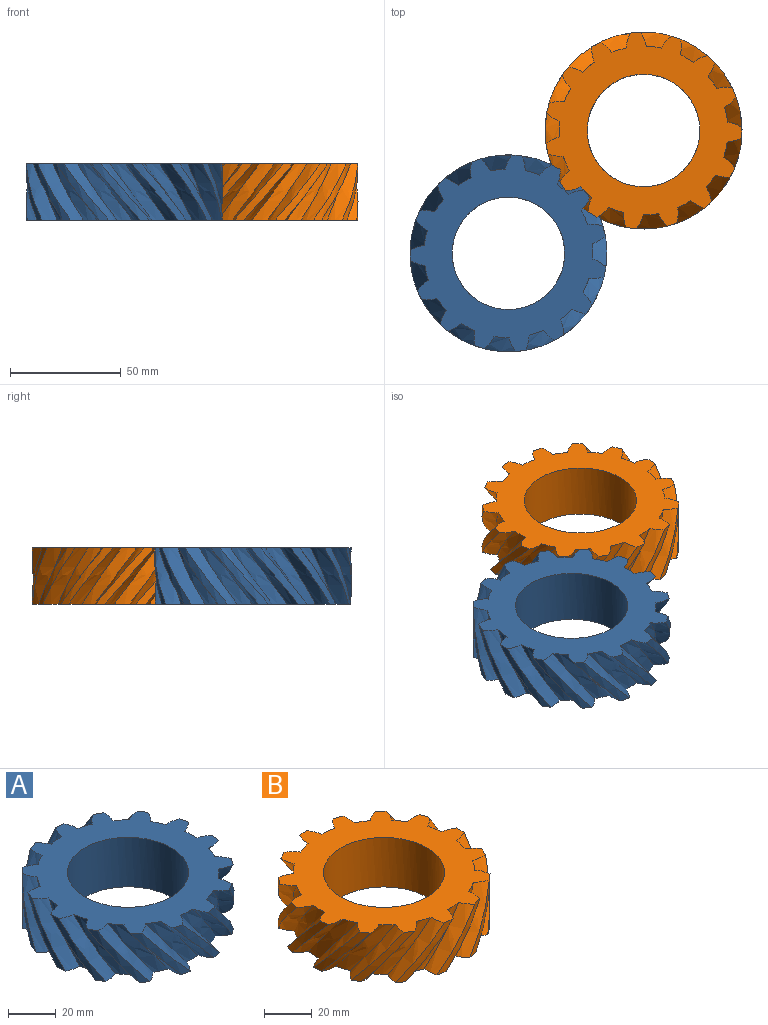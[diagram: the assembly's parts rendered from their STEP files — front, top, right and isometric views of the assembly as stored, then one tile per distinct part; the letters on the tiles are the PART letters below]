
ASSEMBLY  parts=2 mates=1
PART A: 63 faces, bbox 89.7x89.7x26.5 mm
  f0: plane 88.78x88.3mm, normal (0,0,-1), area 3229.3mm2, adj f2,f3,f4,f5,f6,f7,f8,f9
  f1: plane 88.77x88.47mm, normal (0,0,1), area 3228.8mm2, adj f2,f3,f4,f5,f6,f7,f8,f9
  f2: bspline ~26.46x18.66mm, area 176mm2, adj f0,f1,f3,f61
  f3: bspline ~25.4x18.83mm, area 220.5mm2, adj f0,f1,f2,f4
  f4: bspline ~26.46x22.91mm, area 114mm2, adj f0,f1,f3,f5
  f5: bspline ~26.46x24.18mm, area 222.2mm2, adj f0,f1,f4,f6
  f6: bspline ~26.46x24.6mm, area 176mm2, adj f0,f1,f5,f7
  f7: bspline ~26.46x22.82mm, area 220.5mm2, adj f0,f1,f6,f8
  f8: bspline ~26.98x26.46mm, area 114mm2, adj f0,f1,f7,f9
  f9: bspline ~26.46x24.53mm, area 222.2mm2, adj f0,f1,f8,f10
  f10: bspline ~26.46x26.28mm, area 176mm2, adj f0,f1,f9,f11
  f11: bspline ~26.46x24.66mm, area 220.5mm2, adj f0,f1,f10,f12
  f12: bspline ~26.46x26.38mm, area 114mm2, adj f0,f1,f11,f13
  f13: bspline ~25.4x20.98mm, area 222.2mm2, adj f0,f1,f12,f14
  f14: bspline ~26.46x23.42mm, area 176mm2, adj f0,f1,f13,f15
  f15: bspline ~26.46x23.23mm, area 220.5mm2, adj f0,f1,f14,f16
  f16: bspline ~25.4x20.36mm, area 114mm2, adj f0,f1,f15,f17
  f17: bspline ~25.4x20.7mm, area 222.2mm2, adj f0,f1,f16,f18
  f18: bspline ~26.46x20.5mm, area 176mm2, adj f0,f1,f17,f19
  f19: bspline ~26.46x19.95mm, area 220.5mm2, adj f0,f1,f18,f20
  f20: bspline ~26.46x24.34mm, area 114mm2, adj f0,f1,f19,f21
  f21: bspline ~26.46x24.67mm, area 222.2mm2, adj f0,f1,f20,f22
  f22: bspline ~26.46x25.44mm, area 176mm2, adj f0,f1,f21,f23
  f23: bspline ~26.46x23.44mm, area 220.5mm2, adj f0,f1,f22,f24
  f24: bspline ~27.28x26.46mm, area 114mm2, adj f0,f1,f23,f25
  f25: bspline ~26.46x24.18mm, area 222.2mm2, adj f0,f1,f24,f26
  f26: bspline ~26.46x25.99mm, area 176mm2, adj f0,f1,f25,f27
  f27: bspline ~26.46x24.71mm, area 220.5mm2, adj f0,f1,f26,f28
  f28: bspline ~26.46x25.5mm, area 114mm2, adj f0,f1,f27,f29
  f29: bspline ~25.4x20.12mm, area 222.2mm2, adj f0,f1,f28,f30
  f30: bspline ~26.46x22.04mm, area 176mm2, adj f0,f1,f29,f31
  f31: bspline ~26.46x22.22mm, area 220.5mm2, adj f0,f1,f30,f32
  f32: bspline ~26.46x19.31mm, area 114mm2, adj f0,f1,f31,f33
  f33: bspline ~26.46x22.4mm, area 222.2mm2, adj f0,f1,f32,f34
  f34: bspline ~26.46x22.11mm, area 176mm2, adj f0,f1,f33,f35
  f35: bspline ~25.4x20.3mm, area 220.5mm2, adj f0,f1,f34,f36
  f36: bspline ~26.46x25.5mm, area 114mm2, adj f0,f1,f35,f37
  f37: bspline ~25.4x24.11mm, area 222.2mm2, adj f0,f1,f36,f38
  f38: bspline ~26.46x26.01mm, area 176mm2, adj f0,f1,f37,f39
  f39: bspline ~26.46x24.04mm, area 220.5mm2, adj f0,f1,f38,f40
  f40: bspline ~26.37x25.4mm, area 114mm2, adj f0,f1,f39,f41
  f41: bspline ~26.46x23.57mm, area 222.2mm2, adj f0,f1,f40,f42
  f42: bspline ~26.46x25.41mm, area 176mm2, adj f0,f1,f41,f43
  f43: bspline ~25.4x23.69mm, area 220.5mm2, adj f0,f1,f42,f44
  f44: bspline ~25.4x23.42mm, area 114mm2, adj f0,f1,f43,f45
  f45: bspline ~26.46x19.95mm, area 222.2mm2, adj f0,f1,f44,f46
  f46: bspline ~26.46x20.42mm, area 176mm2, adj f0,f1,f45,f47
  f47: bspline ~26.46x20.97mm, area 220.5mm2, adj f0,f1,f46,f48
  f48: bspline ~26.46x21.23mm, area 114mm2, adj f0,f1,f47,f49
  f49: bspline ~26.46x23.41mm, area 222.2mm2, adj f0,f1,f48,f50
  f50: bspline ~26.46x23.48mm, area 176mm2, adj f0,f1,f49,f51
  f51: bspline ~26.46x21.95mm, area 220.5mm2, adj f0,f1,f50,f52
  f52: bspline ~26.46x26.38mm, area 114mm2, adj f0,f1,f51,f53
  f53: bspline ~25.4x24.02mm, area 222.2mm2, adj f0,f1,f52,f54
  f54: bspline ~26.46x26.29mm, area 176mm2, adj f0,f1,f53,f55
  f55: bspline ~25.4x23.57mm, area 220.5mm2, adj f0,f1,f54,f56
  f56: bspline ~26.98x26.46mm, area 114mm2, adj f0,f1,f55,f57
  f57: bspline ~25.4x21.76mm, area 222.2mm2, adj f0,f1,f56,f58
  f58: bspline ~26.46x24.55mm, area 176mm2, adj f0,f1,f57,f59
  f59: bspline ~26.46x23.99mm, area 220.5mm2, adj f0,f1,f58,f60
  f60: bspline ~26.46x22.91mm, area 114mm2, adj f0,f1,f59,f61
  f61: bspline ~25.4x19.3mm, area 222.2mm2, adj f0,f1,f2,f60
  f62: cylinder r=25.4mm len=50.8mm, axis (0,0,-1), area 4053.7mm2, adj f0,f1
PART B: 63 faces, bbox 89.7x89.7x26.5 mm
  f0: plane 88.78x88.3mm, normal (0,0,-1), area 3229.3mm2, adj f2,f3,f4,f5,f6,f7,f8,f9
  f1: plane 88.77x88.47mm, normal (0,0,1), area 3229.2mm2, adj f2,f3,f4,f5,f6,f7,f8,f9
  f2: bspline ~26.46x25.44mm, area 176mm2, adj f0,f1,f3,f61
  f3: bspline ~26.46x23.44mm, area 220.5mm2, adj f0,f1,f2,f4
  f4: bspline ~26.37x25.4mm, area 114mm2, adj f0,f1,f3,f5
  f5: bspline ~26.46x24.18mm, area 222.2mm2, adj f0,f1,f4,f6
  f6: bspline ~26.46x25.99mm, area 176mm2, adj f0,f1,f5,f7
  f7: bspline ~25.4x23.92mm, area 220.5mm2, adj f0,f1,f6,f8
  f8: bspline ~26.46x25.5mm, area 114mm2, adj f0,f1,f7,f9
  f9: bspline ~25.4x20.3mm, area 222.2mm2, adj f0,f1,f8,f10
  f10: bspline ~26.46x22.04mm, area 176mm2, adj f0,f1,f9,f11
  f11: bspline ~25.4x21.71mm, area 220.5mm2, adj f0,f1,f10,f12
  f12: bspline ~26.46x19.31mm, area 114mm2, adj f0,f1,f11,f13
  f13: bspline ~26.46x22.4mm, area 222.2mm2, adj f0,f1,f12,f14
  f14: bspline ~26.46x22.11mm, area 176mm2, adj f0,f1,f13,f15
  f15: bspline ~25.4x20.12mm, area 220.5mm2, adj f0,f1,f14,f16
  f16: bspline ~26.46x25.5mm, area 114mm2, adj f0,f1,f15,f17
  f17: bspline ~26.46x24.9mm, area 222.2mm2, adj f0,f1,f16,f18
  f18: bspline ~26.46x26.01mm, area 176mm2, adj f0,f1,f17,f19
  f19: bspline ~25.4x22.97mm, area 220.5mm2, adj f0,f1,f18,f20
  f20: bspline ~27.28x26.46mm, area 114mm2, adj f0,f1,f19,f21
  f21: bspline ~26.46x23.57mm, area 222.2mm2, adj f0,f1,f20,f22
  f22: bspline ~26.46x25.41mm, area 176mm2, adj f0,f1,f21,f23
  f23: bspline ~26.46x24.48mm, area 220.5mm2, adj f0,f1,f22,f24
  f24: bspline ~26.46x24.34mm, area 114mm2, adj f0,f1,f23,f25
  f25: bspline ~26.46x19.95mm, area 222.2mm2, adj f0,f1,f24,f26
  f26: bspline ~26.46x20.42mm, area 176mm2, adj f0,f1,f25,f27
  f27: bspline ~26.46x20.97mm, area 220.5mm2, adj f0,f1,f26,f28
  f28: bspline ~26.46x21.23mm, area 114mm2, adj f0,f1,f27,f29
  f29: bspline ~26.46x23.41mm, area 222.2mm2, adj f0,f1,f28,f30
  f30: bspline ~26.46x23.48mm, area 176mm2, adj f0,f1,f29,f31
  f31: bspline ~26.46x21.95mm, area 220.5mm2, adj f0,f1,f30,f32
  f32: bspline ~26.46x26.38mm, area 114mm2, adj f0,f1,f31,f33
  f33: bspline ~26.46x24.85mm, area 222.2mm2, adj f0,f1,f32,f34
  f34: bspline ~26.46x26.29mm, area 176mm2, adj f0,f1,f33,f35
  f35: bspline ~26.46x24.38mm, area 220.5mm2, adj f0,f1,f34,f36
  f36: bspline ~26.98x26.46mm, area 114mm2, adj f0,f1,f35,f37
  f37: bspline ~26.46x22.88mm, area 222.2mm2, adj f0,f1,f36,f38
  f38: bspline ~26.46x24.55mm, area 176mm2, adj f0,f1,f37,f39
  f39: bspline ~25.4x23.32mm, area 220.5mm2, adj f0,f1,f38,f40
  f40: bspline ~26.46x22.91mm, area 114mm2, adj f0,f1,f39,f41
  f41: bspline ~25.4x18.99mm, area 222.2mm2, adj f0,f1,f40,f42
  f42: bspline ~26.46x18.66mm, area 176mm2, adj f0,f1,f41,f43
  f43: bspline ~26.46x19.48mm, area 220.5mm2, adj f0,f1,f42,f44
  f44: bspline ~26.46x22.91mm, area 114mm2, adj f0,f1,f43,f45
  f45: bspline ~25.4x23.39mm, area 222.2mm2, adj f0,f1,f44,f46
  f46: bspline ~26.46x24.6mm, area 176mm2, adj f0,f1,f45,f47
  f47: bspline ~25.4x21.71mm, area 220.5mm2, adj f0,f1,f46,f48
  f48: bspline ~26.98x26.46mm, area 114mm2, adj f0,f1,f47,f49
  f49: bspline ~25.4x23.75mm, area 222.2mm2, adj f0,f1,f48,f50
  f50: bspline ~26.46x26.28mm, area 176mm2, adj f0,f1,f49,f51
  f51: bspline ~26.46x24.66mm, area 220.5mm2, adj f0,f1,f50,f52
  f52: bspline ~25.59x25.4mm, area 114mm2, adj f0,f1,f51,f53
  f53: bspline ~26.46x22.02mm, area 222.2mm2, adj f0,f1,f52,f54
  f54: bspline ~26.46x23.42mm, area 176mm2, adj f0,f1,f53,f55
  f55: bspline ~26.46x23.23mm, area 220.5mm2, adj f0,f1,f54,f56
  f56: bspline ~26.46x21.23mm, area 114mm2, adj f0,f1,f55,f57
  f57: bspline ~26.46x21.13mm, area 222.2mm2, adj f0,f1,f56,f58
  f58: bspline ~26.46x20.5mm, area 176mm2, adj f0,f1,f57,f59
  f59: bspline ~26.46x19.95mm, area 220.5mm2, adj f0,f1,f58,f60
  f60: bspline ~25.4x23.42mm, area 114mm2, adj f0,f1,f59,f61
  f61: bspline ~26.46x24.67mm, area 222.2mm2, adj f0,f1,f2,f60
  f62: cylinder r=25.4mm len=50.8mm, axis (0,0,-1), area 4053.7mm2, adj f0,f1
PLACE A t=(-63.07,-51.96,-5.58)mm
PLACE B t=(-2.03,3.48,-5.58)mm
MATE planar A.f62 <-> B.f1  axis (0,0,1) through (-63.07,-51.96,19.82)mm
